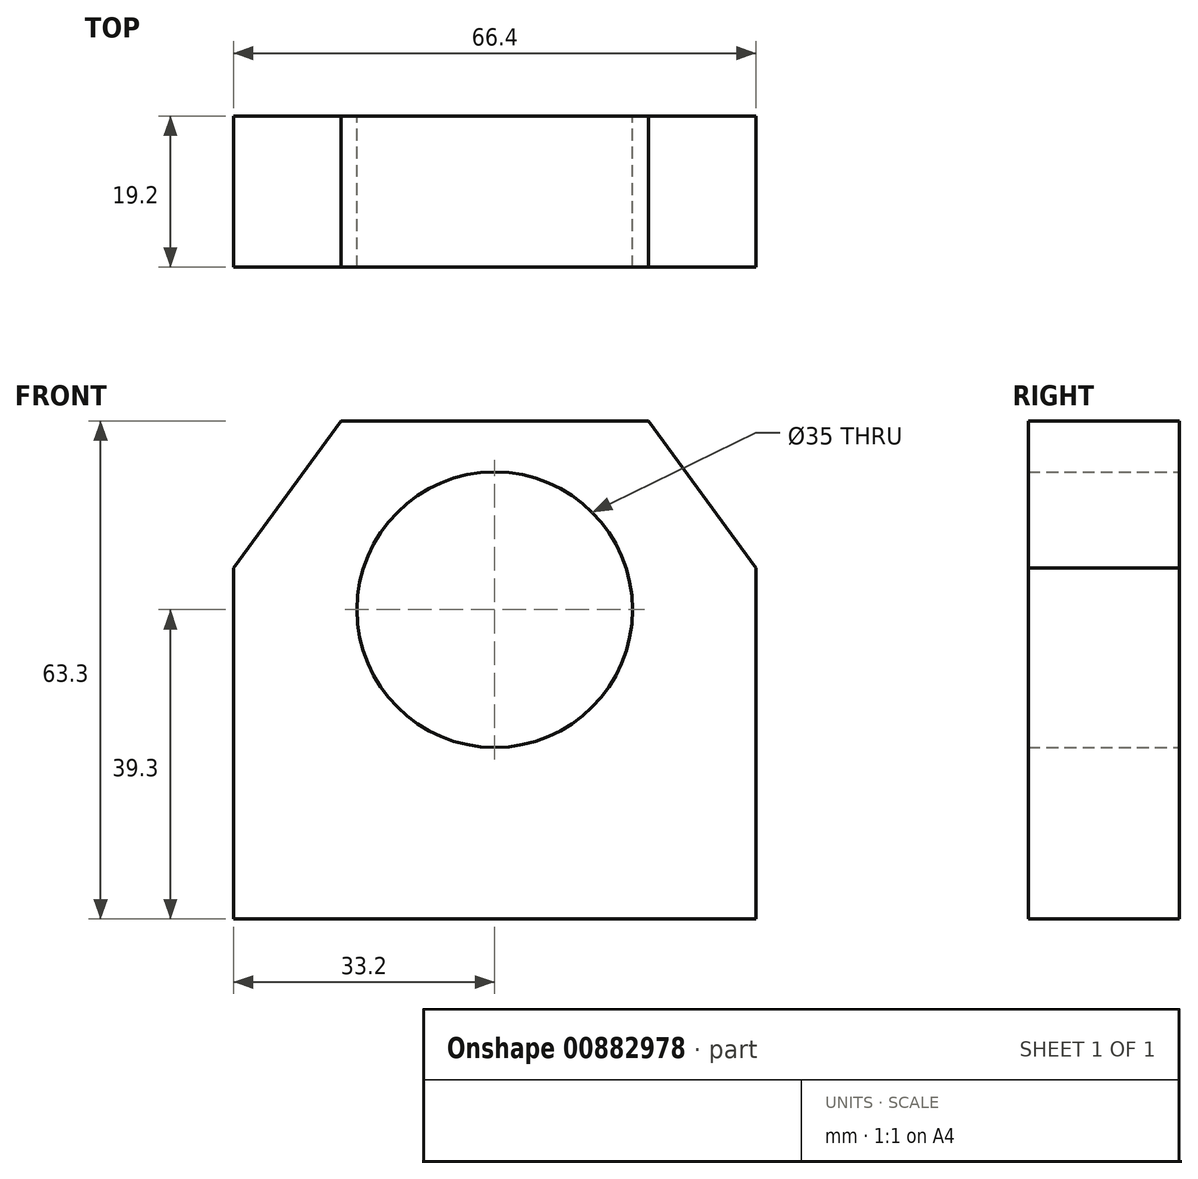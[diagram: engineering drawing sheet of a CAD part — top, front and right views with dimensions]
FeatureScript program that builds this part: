
annotation { "Feature Type Name" : "Feature", "Feature Type Description" : "" }
export const myFeature = defineFeature(function(context is Context, id is Id, definition is map)
    precondition{}
    {
        {
            var Q0;
            Q0=qCreatedBy(makeId("Front.planeOp"),FACE);
            var sketch = newSketch(context, id + "F0", { "sketchPlane" : qUnion([Q0])});
            skLineSegment(sketch, "E0", {"start": v(0, 0) * mm, "end": v(-33.2, 0) * mm});
            skLineSegment(sketch, "E1", {"start": v(-33.2, 0) * mm, "end": v(-33.2, 44.6) * mm});
            skLineSegment(sketch, "E2", {"start": v(-33.2, 44.6) * mm, "end": v(-19.5, 63.3) * mm});
            skLineSegment(sketch, "E3", {"start": v(-19.5, 63.3) * mm, "end": v(0, 63.3) * mm});
            skLineSegment(sketch, "E4.MirrorCS", {"start": v(19.5, 63.3) * mm, "end": v(0, 63.3) * mm});
            skLineSegment(sketch, "E5.MirrorCS", {"start": v(33.2, 44.6) * mm, "end": v(19.5, 63.3) * mm});
            skLineSegment(sketch, "E6.MirrorCS", {"start": v(33.2, 0) * mm, "end": v(33.2, 44.6) * mm});
            skLineSegment(sketch, "E7.MirrorCS", {"start": v(0, 0) * mm, "end": v(33.2, 0) * mm});
            skCircle(sketch, "E8", {"center": v(0, 39.3) * mm, "radius": 17.5 * mm});
            skSolve(sketch);
        }
        {
            var Q0;
            Q0=makeQuery(id+"F0.imprint","IMPRINT",FACE,{"disambiguationData":[TD([[makeQuery(id+"F0.imprint","IMPRINT",EDGE,{"derivedFrom":sQuery(id+"F0.wireOp",EDGE,"E0")}),-1.0]])]});
            extrude(context, id + "F1", {"entities" : qUnion([Q0]), "depth" : 19.2 * mm, "offsetDistance" : 25 * mm});
        }
    });
